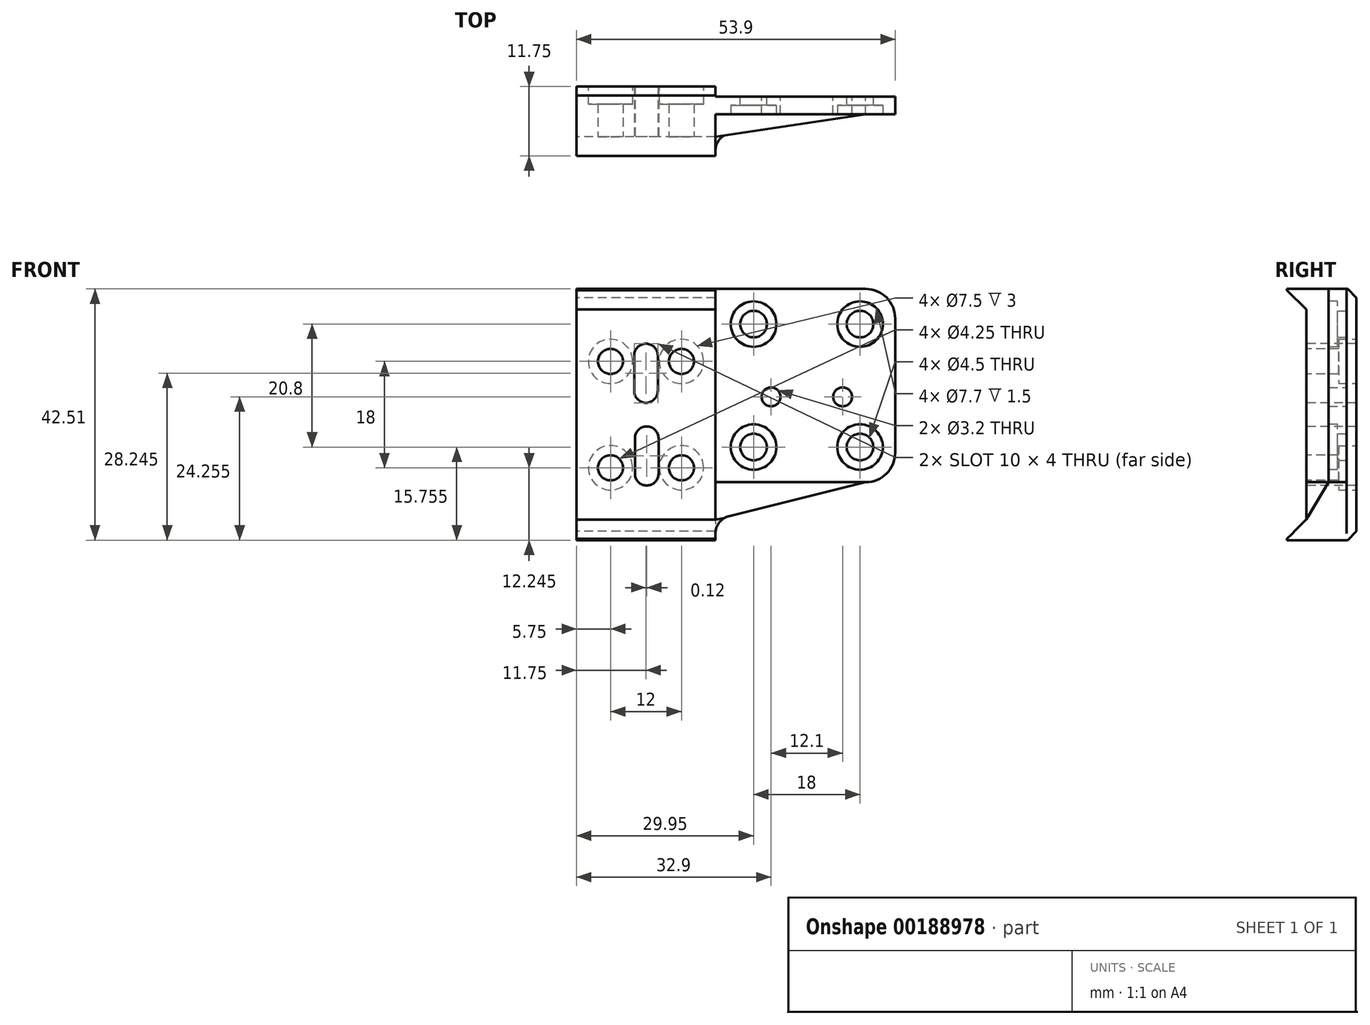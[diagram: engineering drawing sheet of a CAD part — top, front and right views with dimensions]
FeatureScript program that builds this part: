
annotation { "Feature Type Name" : "Feature", "Feature Type Description" : "" }
export const myFeature = defineFeature(function(context is Context, id is Id, definition is map)
    precondition{}
    {
        {
            var Q0;
            Q0=qCreatedBy(makeId("Front.planeOp"),FACE);
            var sketch = newSketch(context, id + "F0", { "sketchPlane" : qUnion([Q0])});
            skLineSegment(sketch, "E0.bottom", {"start": v(11.75, -21.26) * mm, "end": v(-11.75, -21.26) * mm});
            skLineSegment(sketch, "E0.top", {"start": v(11.75, 21.25) * mm, "end": v(-11.75, 21.25) * mm});
            skLineSegment(sketch, "E0.left", {"start": v(11.75, -21.25) * mm, "end": v(11.75, 21.26) * mm});
            skLineSegment(sketch, "E0.right", {"start": v(-11.75, -21.26) * mm, "end": v(-11.75, 21.25) * mm});
            skPoint(sketch, "E0.middle", {"position": v(0, 0) * mm});
            skSolve(sketch);
        }
        {
            var Q0;
            Q0=qSketchRegion(id+"F0",true);
            extrude(context, id + "F1", {"entities" : qUnion([Q0]), "depth" : 9 * mm});
        }
        {
            var Q0;
            Q0=makeQuery(id+"F1.opExtrude","CAP_FACE",FACE,{"disambiguationData":[OSD([sQuery(id+"F0.wireOp",EDGE,"E0.bottom"),sQuery(id+"F0.wireOp",EDGE,"E0.top"),sQuery(id+"F0.wireOp",EDGE,"E0.left"),sQuery(id+"F0.wireOp",EDGE,"E0.right")])],"isStart":false});
            var sketch = newSketch(context, id + "F2", { "sketchPlane" : qUnion([Q0])});
            skCircle(sketch, "E1", {"center": v(-6, 9) * mm, "radius": 2.12 * mm});
            skCircle(sketch, "E2.1.0.0", {"center": v(6, 9) * mm, "radius": 2.12 * mm});
            skLineSegment(sketch, "E2.direction1", {"start": v(-6, 9) * mm, "end": v(6, 9) * mm, "construction": true});
            skCircle(sketch, "E3.1.0.0", {"center": v(-6, -9) * mm, "radius": 2.12 * mm});
            skCircle(sketch, "E3.1.0.1", {"center": v(6, -9) * mm, "radius": 2.12 * mm});
            skLineSegment(sketch, "E3.direction1", {"start": v(-6, -9) * mm, "end": v(-6, 9) * mm, "construction": true});
            skArc(sketch, "E4", {"start": v(2, 10) * mm, "mid": v(0, 12) * mm, "end": v(-2, 10) * mm});
            skLineSegment(sketch, "E5.left", {"start": v(2, 10) * mm, "end": v(2, 4) * mm});
            skLineSegment(sketch, "E5.right", {"start": v(-2, 10) * mm, "end": v(-2, 4) * mm});
            skArc(sketch, "E6", {"start": v(-2, 4) * mm, "mid": v(0, 2) * mm, "end": v(2, 4) * mm});
            skArc(sketch, "E7.1.0.0", {"start": v(2.12, -4) * mm, "mid": v(0.12, -2) * mm, "end": v(-1.88, -4) * mm});
            skLineSegment(sketch, "E7.1.0.1", {"start": v(2.12, -4) * mm, "end": v(2.12, -10) * mm});
            skArc(sketch, "E7.1.0.2", {"start": v(-1.88, -10) * mm, "mid": v(0.12, -12) * mm, "end": v(2.12, -10) * mm});
            skLineSegment(sketch, "E7.1.0.3", {"start": v(-1.88, -4) * mm, "end": v(-1.88, -10) * mm});
            skLineSegment(sketch, "E7.direction1", {"start": v(-2, 10) * mm, "end": v(-1.88, -4) * mm, "construction": true});
            skSolve(sketch);
        }
        {
            var Q0;
            Q0=makeQuery(id+"F2.imprint","IMPRINT",FACE,{"disambiguationData":[TD([[makeQuery(id+"F2.imprint","IMPRINT",EDGE,{"derivedFrom":sQuery(id+"F2.wireOp",EDGE,"E1")}),1.0]])]});
            var Q1;
            Q1=makeQuery(id+"F2.imprint","IMPRINT",FACE,{"disambiguationData":[TD([[makeQuery(id+"F2.imprint","IMPRINT",EDGE,{"derivedFrom":sQuery(id+"F2.wireOp",EDGE,"E4")}),1.0]])]});
            var Q2;
            Q2=makeQuery(id+"F2.imprint","IMPRINT",FACE,{"disambiguationData":[TD([[makeQuery(id+"F2.imprint","IMPRINT",EDGE,{"derivedFrom":sQuery(id+"F2.wireOp",EDGE,"E2.1.0.0")}),1.0]])]});
            var Q3;
            Q3=makeQuery(id+"F2.imprint","IMPRINT",FACE,{"disambiguationData":[TD([[makeQuery(id+"F2.imprint","IMPRINT",EDGE,{"derivedFrom":sQuery(id+"F2.wireOp",EDGE,"E3.1.0.1")}),1.0]])]});
            var Q4;
            Q4=makeQuery(id+"F2.imprint","IMPRINT",FACE,{"disambiguationData":[TD([[makeQuery(id+"F2.imprint","IMPRINT",EDGE,{"derivedFrom":sQuery(id+"F2.wireOp",EDGE,"E7.1.0.0")}),1.0]])]});
            var Q5;
            Q5=makeQuery(id+"F2.imprint","IMPRINT",FACE,{"disambiguationData":[TD([[makeQuery(id+"F2.imprint","IMPRINT",EDGE,{"derivedFrom":sQuery(id+"F2.wireOp",EDGE,"E3.1.0.0")}),1.0]])]});
            extrude(context, id + "F3", {"entities" : qUnion([Q0, Q1, Q2, Q3, Q4, Q5]), "operationType" : NewBodyOperationType.REMOVE, "endBound" : BoundingType.THROUGH_ALL, "oppositeDirection" : true, "depth" : 25 * mm});
        }
        {
            var Q0;
            Q0=makeQuery(id+"F1.opExtrude","SWEPT_FACE",FACE,{"disambiguationData":[OSD([sQuery(id+"F0.wireOp",EDGE,"E0.right")])]});
            var sketch = newSketch(context, id + "F4", { "sketchPlane" : qUnion([Q0])});
            skLineSegment(sketch, "E8", {"start": v(9, 21.25) * mm, "end": v(12.25, 21.25) * mm});
            skLineSegment(sketch, "E9", {"start": v(12.25, 21.25) * mm, "end": v(12.25, 21) * mm});
            skLineSegment(sketch, "E10", {"start": v(12.25, 21) * mm, "end": v(9, 17.75) * mm});
            skLineSegment(sketch, "E11", {"start": v(9, 17.75) * mm, "end": v(9, 21.25) * mm});
            skLineSegment(sketch, "E12", {"start": v(0, 0) * mm, "end": v(9, 0) * mm});
            skLineSegment(sketch, "E13.MirrorCS", {"start": v(9, -21.26) * mm, "end": v(12.25, -21.26) * mm});
            skLineSegment(sketch, "E14.MirrorCS", {"start": v(9, -17.76) * mm, "end": v(9, -21.26) * mm});
            skLineSegment(sketch, "E15.MirrorCS", {"start": v(12.25, -21) * mm, "end": v(9, -17.76) * mm});
            skLineSegment(sketch, "E16.MirrorCS", {"start": v(12.25, -21.26) * mm, "end": v(12.25, -21) * mm});
            skSolve(sketch);
        }
        {
            var Q0;
            Q0=makeQuery(id+"F4.imprint","IMPRINT",FACE,{"disambiguationData":[TD([[makeQuery(id+"F4.imprint","IMPRINT",EDGE,{"derivedFrom":sQuery(id+"F4.wireOp",EDGE,"E8")}),-1.0]])]});
            var Q1;
            Q1=makeQuery(id+"F4.imprint","IMPRINT",FACE,{"disambiguationData":[TD([[makeQuery(id+"F4.imprint","IMPRINT",EDGE,{"derivedFrom":sQuery(id+"F4.wireOp",EDGE,"E13.MirrorCS")}),1.0]])]});
            extrude(context, id + "F5", {"entities" : qUnion([Q0, Q1]), "operationType" : NewBodyOperationType.ADD, "oppositeDirection" : true, "depth" : 23.5 * mm});
        }
        {
            var Q0;
            Q0=makeQuery(id+"F1.opExtrude","CAP_EDGE",EDGE,{"disambiguationData":[OSD([sQuery(id+"F0.wireOp",EDGE,"E0.top")])],"isStart":true});
            var Q1;
            Q1=makeQuery(id+"F1.opExtrude","CAP_EDGE",EDGE,{"disambiguationData":[OSD([sQuery(id+"F0.wireOp",EDGE,"E0.bottom")])],"isStart":true});
            chamfer(context, id + "F6", {"entities" : qUnion([Q0, Q1]), "width" : 2 * mm, "tangentPropagation" : true});
        }
        {
            var Q0;
            Q0=qCreatedBy(makeId("Front.planeOp"),FACE);
            cPlane(context, id + "F7", {"entities" : qUnion([Q0]), "cplaneType" : CPlaneType.OFFSET, "offset" : 2.2 * mm, "width" : 150 * mm, "height" : 150 * mm});
        }
        {
            var Q0;
            Q0=qCreatedBy(id+"F7.planeOp",FACE);
            var sketch = newSketch(context, id + "F8", { "sketchPlane" : qUnion([Q0])});
            skCircle(sketch, "E17", {"center": v(18.2, -5.5) * mm, "radius": 2.25 * mm});
            skCircle(sketch, "E18.0.1.0", {"center": v(18.2, 15.3) * mm, "radius": 2.25 * mm});
            skCircle(sketch, "E18.1.0.0", {"center": v(36.2, -5.5) * mm, "radius": 2.25 * mm});
            skCircle(sketch, "E18.1.1.0", {"center": v(36.2, 15.3) * mm, "radius": 2.25 * mm});
            skLineSegment(sketch, "E18.direction1", {"start": v(18.2, -5.5) * mm, "end": v(36.2, -5.5) * mm, "construction": true});
            skLineSegment(sketch, "E18.direction2", {"start": v(18.2, -5.5) * mm, "end": v(18.2, 15.3) * mm, "construction": true});
            skCircle(sketch, "E19", {"center": v(33.25, 3) * mm, "radius": 1.6 * mm});
            skCircle(sketch, "E20.1.0.0", {"center": v(21.15, 3) * mm, "radius": 1.6 * mm});
            skLineSegment(sketch, "E20.direction1", {"start": v(33.25, 3) * mm, "end": v(21.15, 3) * mm, "construction": true});
            skSolve(sketch);
        }
        {
            var Q0;
            Q0=qCreatedBy(id+"F7.planeOp",FACE);
            var sketch = newSketch(context, id + "F9", { "sketchPlane" : qUnion([Q0])});
            skLineSegment(sketch, "E21.bottom", {"start": v(11.75, 21.25) * mm, "end": v(37.15, 21.25) * mm});
            skLineSegment(sketch, "E21.top", {"start": v(11.75, -11.44) * mm, "end": v(37.15, -11.44) * mm});
            skLineSegment(sketch, "E21.left", {"start": v(11.75, 21.25) * mm, "end": v(11.75, -11.44) * mm});
            skLineSegment(sketch, "E21.right", {"start": v(42.15, 16.25) * mm, "end": v(42.15, -6.44) * mm});
            skLineSegment(sketch, "E22", {"start": v(42.15, 4.9) * mm, "end": v(36.2, 4.9) * mm, "construction": true});
            skLineSegment(sketch, "E23", {"start": v(36.2, 15.3) * mm, "end": v(36.2, -5.5) * mm, "construction": true});
            skCircle(sketch, "E24", {"center": v(36.2, 15.3) * mm, "radius": 5.95 * mm, "construction": true});
            skPoint(sketch, "E25.visualSharp", {"position": v(42.15, 21.25) * mm});
            skArc(sketch, "E25.filletArc", {"start": v(42.15, 16.25) * mm, "mid": v(40.69, 19.8) * mm, "end": v(37.15, 21.25) * mm});
            skPoint(sketch, "E26.visualSharp", {"position": v(42.15, -11.44) * mm});
            skArc(sketch, "E26.filletArc", {"start": v(37.15, -11.44) * mm, "mid": v(40.69, -9.98) * mm, "end": v(42.15, -6.44) * mm});
            skSolve(sketch);
        }
        {
            var Q0;
            Q0 = qSketchRegion(id + "F9", true);
            extrude(context, id + "F10", {"entities" : qUnion([Q0]), "operationType" : NewBodyOperationType.ADD, "depth" : 3 * mm});
        }
        {
            var Q0;
            Q0 = qSketchRegion(id + "F8", true);
            extrude(context, id + "F11", {"entities" : qUnion([Q0]), "operationType" : NewBodyOperationType.REMOVE, "depth" : 25 * mm});
        }
        {
            var Q0;
            Q0=makeQuery(id+"F8.imprint","IMPRINT",FACE,{"disambiguationData":[TD([[makeQuery(id+"F8.imprint","IMPRINT",EDGE,{"derivedFrom":sQuery(id+"F8.wireOp",EDGE,"E18.0.1.0")}),1.0]])]});
            var Q1;
            Q1=makeQuery(id+"F8.imprint","IMPRINT",FACE,{"disambiguationData":[TD([[makeQuery(id+"F8.imprint","IMPRINT",EDGE,{"derivedFrom":sQuery(id+"F8.wireOp",EDGE,"E18.1.1.0")}),1.0]])]});
            var Q2;
            Q2=makeQuery(id+"F8.imprint","IMPRINT",FACE,{"disambiguationData":[TD([[makeQuery(id+"F8.imprint","IMPRINT",EDGE,{"derivedFrom":sQuery(id+"F8.wireOp",EDGE,"E20.1.0.0")}),1.0]])]});
            var Q3;
            Q3=makeQuery(id+"F8.imprint","IMPRINT",FACE,{"disambiguationData":[TD([[makeQuery(id+"F8.imprint","IMPRINT",EDGE,{"derivedFrom":sQuery(id+"F8.wireOp",EDGE,"E19")}),1.0]])]});
            var Q4;
            Q4=makeQuery(id+"F8.imprint","IMPRINT",FACE,{"disambiguationData":[TD([[makeQuery(id+"F8.imprint","IMPRINT",EDGE,{"derivedFrom":sQuery(id+"F8.wireOp",EDGE,"E17")}),1.0]])]});
            var Q5;
            Q5=makeQuery(id+"F8.imprint","IMPRINT",FACE,{"disambiguationData":[TD([[makeQuery(id+"F8.imprint","IMPRINT",EDGE,{"derivedFrom":sQuery(id+"F8.wireOp",EDGE,"E18.1.0.0")}),1.0]])]});
            extrude(context, id + "F12", {"entities" : qUnion([Q0, Q1, Q2, Q3, Q4, Q5]), "operationType" : NewBodyOperationType.REMOVE, "endBound" : BoundingType.THROUGH_ALL, "oppositeDirection" : true, "depth" : 25 * mm});
        }
        {
            var Q0;
            Q0=makeQuery(id+"F10.opExtrude","SWEPT_FACE",FACE,{"disambiguationData":[OSD([sQuery(id+"F9.wireOp",EDGE,"E21.top")])]});
            var sketch = newSketch(context, id + "F13", { "sketchPlane" : qUnion([Q0])});
            skLineSegment(sketch, "E27.0.0", {"start": v(11.75, 2.2) * mm, "end": v(37.15, 2.2) * mm});
            skLineSegment(sketch, "E27.0.1", {"start": v(37.15, 2.2) * mm, "end": v(37.15, 5.2) * mm});
            skLineSegment(sketch, "E27.0.3", {"start": v(11.75, 5.2) * mm, "end": v(11.75, 2.2) * mm});
            skLineSegment(sketch, "E28", {"start": v(11.75, 9) * mm, "end": v(37.15, 5.2) * mm});
            skLineSegment(sketch, "E29", {"start": v(11.75, 5.2) * mm, "end": v(11.75, 9) * mm});
            skSolve(sketch);
        }
        {
            var Q0;
            Q0 = qSketchRegion(id + "F13", true);
            var Q1;
            Q1=makeQuery(id+"F5.opExtrude","CAP_VERTEX",VERTEX,{"disambiguationData":[OSD([sQuery(id+"F0.wireOp",EDGE,"E0.right"),sQuery(id+"F4.wireOp",EDGE,"E14.MirrorCS"),sQuery(id+"F4.wireOp",EDGE,"E15.MirrorCS")])],"isStart":false});
            extrude(context, id + "F14", {"entities" : qUnion([Q0]), "operationType" : NewBodyOperationType.ADD, "endBound" : BoundingType.UP_TO_VERTEX, "endBoundEntityVertex" : qUnion([Q1]), "depth" : 3 * mm});
        }
        {
            var Q0;
            Q0=makeQuery(id+"F14.boolean.opBoolean","MERGE",FACE,{"derivedFrom":[makeQuery(id+"F10.opExtrude","CAP_FACE",FACE,{"disambiguationData":[OSD([sQuery(id+"F9.wireOp",EDGE,"E21.bottom"),sQuery(id+"F9.wireOp",EDGE,"E21.top"),sQuery(id+"F9.wireOp",EDGE,"E21.left"),sQuery(id+"F9.wireOp",EDGE,"E21.right"),sQuery(id+"F9.wireOp",EDGE,"E25.filletArc"),sQuery(id+"F9.wireOp",EDGE,"E26.filletArc")])],"isStart":true}),makeQuery(id+"F14.opExtrude","SWEPT_FACE",FACE,{"disambiguationData":[OSD([sQuery(id+"F13.wireOp",EDGE,"E27.0.0")])]})]});
            var sketch = newSketch(context, id + "F15", { "sketchPlane" : qUnion([Q0])});
            skLineSegment(sketch, "E30", {"start": v(-37.15, -11.44) * mm, "end": v(-11.75, -17.76) * mm});
            skLineSegment(sketch, "E31", {"start": v(-11.75, -17.76) * mm, "end": v(-37.15, -17.76) * mm});
            skLineSegment(sketch, "E32", {"start": v(-37.15, -17.76) * mm, "end": v(-37.15, -11.44) * mm});
            skSolve(sketch);
        }
        {
            var Q0;
            Q0 = qSketchRegion(id + "F15", true);
            extrude(context, id + "F16", {"entities" : qUnion([Q0]), "operationType" : NewBodyOperationType.REMOVE, "oppositeDirection" : true, "depth" : 25 * mm});
        }
        {
            var Q0;
            Q0=makeQuery(id+"F10.opExtrude","CAP_FACE",FACE,{"disambiguationData":[OSD([sQuery(id+"F9.wireOp",EDGE,"E21.bottom"),sQuery(id+"F9.wireOp",EDGE,"E21.top"),sQuery(id+"F9.wireOp",EDGE,"E21.left"),sQuery(id+"F9.wireOp",EDGE,"E21.right"),sQuery(id+"F9.wireOp",EDGE,"E25.filletArc"),sQuery(id+"F9.wireOp",EDGE,"E26.filletArc")])],"isStart":false});
            var sketch = newSketch(context, id + "F17", { "sketchPlane" : qUnion([Q0])});
            skCircle(sketch, "E33", {"center": v(18.2, 15.3) * mm, "radius": 3.85 * mm});
            skCircle(sketch, "E34", {"center": v(36.2, 15.3) * mm, "radius": 3.85 * mm});
            skCircle(sketch, "E35", {"center": v(36.2, -5.5) * mm, "radius": 3.85 * mm});
            skCircle(sketch, "E36", {"center": v(18.2, -5.5) * mm, "radius": 3.85 * mm});
            skSolve(sketch);
        }
        {
            var Q0;
            Q0=makeQuery(id+"F17.imprint","IMPRINT",FACE,{"disambiguationData":[TD([[makeQuery(id+"F17.imprint","IMPRINT",EDGE,{"derivedFrom":sQuery(id+"F17.wireOp",EDGE,"E33")}),1.0]])]});
            var Q1;
            Q1=makeQuery(id+"F17.imprint","IMPRINT",FACE,{"disambiguationData":[TD([[makeQuery(id+"F17.imprint","IMPRINT",EDGE,{"derivedFrom":sQuery(id+"F17.wireOp",EDGE,"E34")}),1.0]])]});
            var Q2;
            Q2=makeQuery(id+"F17.imprint","IMPRINT",FACE,{"disambiguationData":[TD([[makeQuery(id+"F17.imprint","IMPRINT",EDGE,{"derivedFrom":sQuery(id+"F17.wireOp",EDGE,"E35")}),1.0]])]});
            var Q3;
            Q3=makeQuery(id+"F17.imprint","IMPRINT",FACE,{"disambiguationData":[TD([[makeQuery(id+"F17.imprint","IMPRINT",EDGE,{"derivedFrom":sQuery(id+"F17.wireOp",EDGE,"E36")}),1.0]])]});
            extrude(context, id + "F18", {"entities" : qUnion([Q0, Q1, Q2, Q3]), "operationType" : NewBodyOperationType.REMOVE, "oppositeDirection" : true, "depth" : 1.5 * mm});
        }
        {
            var Q0;
            Q0=makeQuery(id+"F10.opExtrude","CAP_EDGE",EDGE,{"disambiguationData":[OSD([sQuery(id+"F9.wireOp",EDGE,"E21.left")])],"isStart":false});
            var Q1;
            {var subQ0=sQuery(id+"F13.wireOp",EDGE,"E27.0.3");Q1=makeQuery(id+"F16.boolean.opBoolean","MERGE",EDGE,{"derivedFrom":[makeQuery(id+"F14.opExtrude","CAP_EDGE",EDGE,{"disambiguationData":[OSD([subQ0,sQuery(id+"F13.wireOp",EDGE,"E29")])],"isStart":false})],"fromTools":[makeQuery(id+"F16.opExtrude","SWEPT_EDGE",EDGE,{"disambiguationData":[OSD([sQuery(id+"F9.wireOp",EDGE,"E21.left"),sQuery(id+"F13.wireOp",EDGE,"E27.0.0"),subQ0,sQuery(id+"F15.wireOp",EDGE,"E30"),sQuery(id+"F15.wireOp",EDGE,"E31")])]})]});}
            fillet(context, id + "F19", {"entities" : qUnion([Q0, Q1]), "radius" : 3 * mm, "tangentPropagation" : true, "allowEdgeOverflow" : false});
        }
        {
            var Q0;
            Q0=makeQuery(id+"F1.opExtrude","CAP_FACE",FACE,{"disambiguationData":[OSD([sQuery(id+"F0.wireOp",EDGE,"E0.bottom"),sQuery(id+"F0.wireOp",EDGE,"E0.top"),sQuery(id+"F0.wireOp",EDGE,"E0.left"),sQuery(id+"F0.wireOp",EDGE,"E0.right")])],"isStart":true});
            var sketch = newSketch(context, id + "F20", { "sketchPlane" : qUnion([Q0])});
            skCircle(sketch, "E37", {"center": v(-6, 9) * mm, "radius": 3.75 * mm});
            skCircle(sketch, "E38", {"center": v(6, 9) * mm, "radius": 3.75 * mm});
            skCircle(sketch, "E39", {"center": v(6, -9) * mm, "radius": 3.75 * mm});
            skCircle(sketch, "E40", {"center": v(-6, -9) * mm, "radius": 3.75 * mm});
            skSolve(sketch);
        }
        {
            var Q0;
            Q0=makeQuery(id+"F20.imprint","IMPRINT",FACE,{"disambiguationData":[TD([[makeQuery(id+"F20.imprint","IMPRINT",EDGE,{"derivedFrom":sQuery(id+"F20.wireOp",EDGE,"E37")}),1.0]])]});
            var Q1;
            Q1=makeQuery(id+"F20.imprint","IMPRINT",FACE,{"disambiguationData":[TD([[makeQuery(id+"F20.imprint","IMPRINT",EDGE,{"derivedFrom":sQuery(id+"F20.wireOp",EDGE,"E38")}),1.0]])]});
            var Q2;
            Q2=makeQuery(id+"F20.imprint","IMPRINT",FACE,{"disambiguationData":[TD([[makeQuery(id+"F20.imprint","IMPRINT",EDGE,{"derivedFrom":sQuery(id+"F20.wireOp",EDGE,"E40")}),1.0]])]});
            var Q3;
            Q3=makeQuery(id+"F20.imprint","IMPRINT",FACE,{"disambiguationData":[TD([[makeQuery(id+"F20.imprint","IMPRINT",EDGE,{"derivedFrom":sQuery(id+"F20.wireOp",EDGE,"E39")}),1.0]])]});
            extrude(context, id + "F21", {"entities" : qUnion([Q0, Q1, Q2, Q3]), "operationType" : NewBodyOperationType.REMOVE, "oppositeDirection" : true, "depth" : 3.5 * mm});
        }
        {
            var Q0;
            Q0=makeQuery(id+"F5.boolean.opBoolean","MERGE",FACE,{"derivedFrom":[makeQuery(id+"F1.opExtrude","SWEPT_FACE",FACE,{"disambiguationData":[OSD([sQuery(id+"F0.wireOp",EDGE,"E0.right")])]}),makeQuery(id+"F5.opExtrude","CAP_FACE",FACE,{"disambiguationData":[OSD([sQuery(id+"F4.wireOp",EDGE,"E8"),sQuery(id+"F4.wireOp",EDGE,"E9"),sQuery(id+"F4.wireOp",EDGE,"E10"),sQuery(id+"F4.wireOp",EDGE,"E11")])],"isStart":true}),makeQuery(id+"F5.opExtrude","CAP_FACE",FACE,{"disambiguationData":[OSD([sQuery(id+"F4.wireOp",EDGE,"E13.MirrorCS"),sQuery(id+"F4.wireOp",EDGE,"E14.MirrorCS"),sQuery(id+"F4.wireOp",EDGE,"E15.MirrorCS"),sQuery(id+"F4.wireOp",EDGE,"E16.MirrorCS")])],"isStart":true})]});
            var sketch = newSketch(context, id + "F22", { "sketchPlane" : qUnion([Q0])});
            skLineSegment(sketch, "E41", {"start": v(0.5, 19.75) * mm, "end": v(0.5, -19.76) * mm});
            skLineSegment(sketch, "E42", {"start": v(0.5, -19.76) * mm, "end": v(0, -19.26) * mm});
            skLineSegment(sketch, "E43", {"start": v(0, -19.26) * mm, "end": v(0, 19.26) * mm});
            skLineSegment(sketch, "E44", {"start": v(0, 19.26) * mm, "end": v(0.5, 19.75) * mm});
            skSolve(sketch);
        }
        {
            var Q0;
            Q0=qSketchRegion(id+"F22",true);
            extrude(context, id + "F23", {"entities" : qUnion([Q0]), "operationType" : NewBodyOperationType.REMOVE, "endBound" : BoundingType.THROUGH_ALL, "oppositeDirection" : true, "depth" : 25 * mm});
        }
    });
